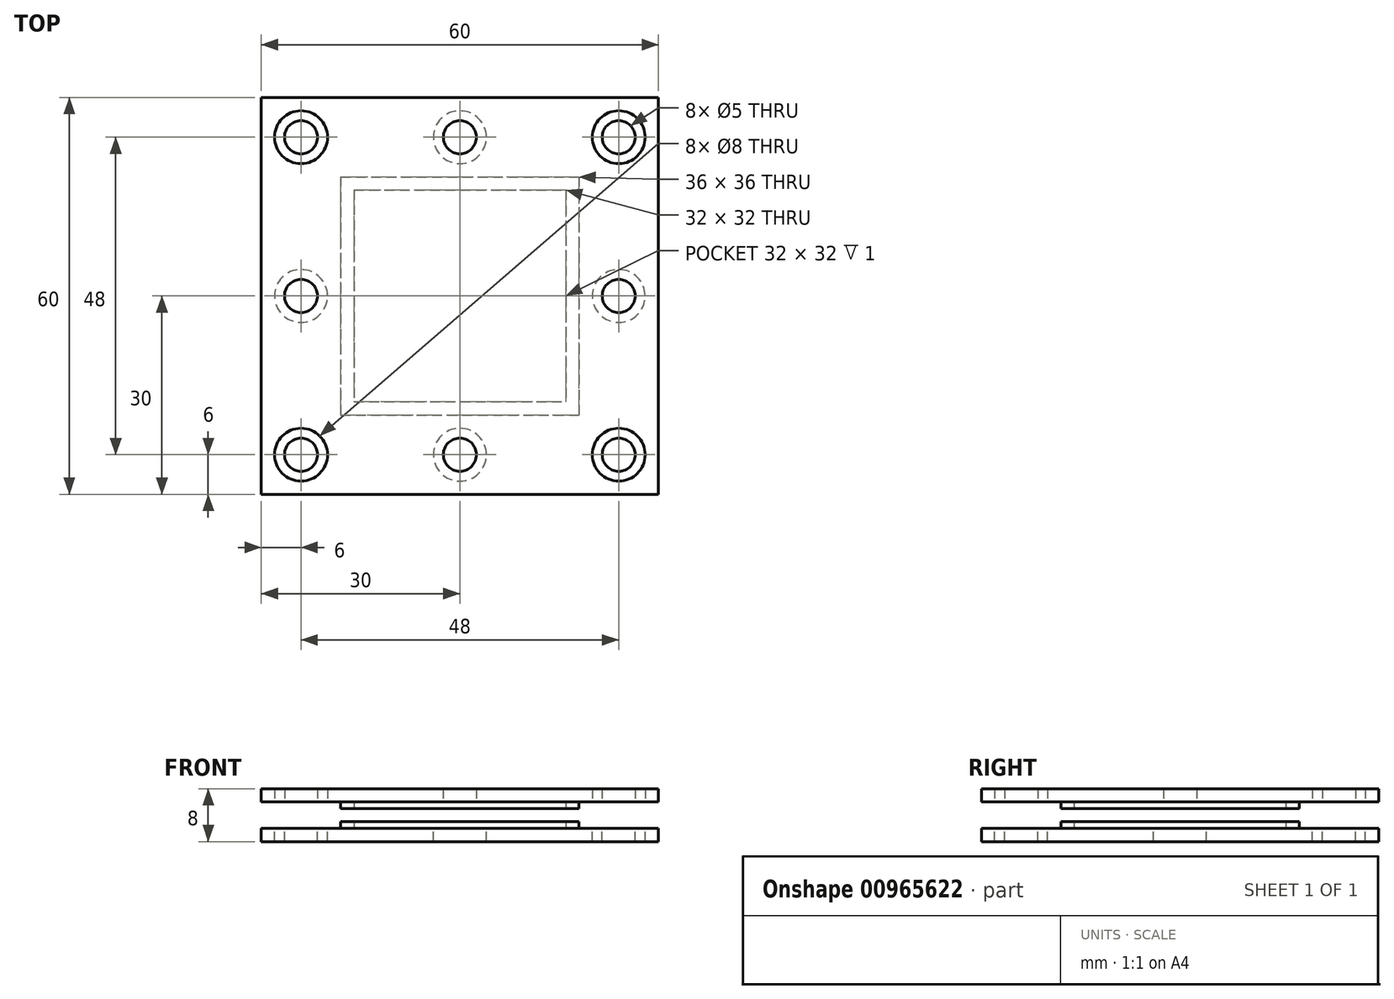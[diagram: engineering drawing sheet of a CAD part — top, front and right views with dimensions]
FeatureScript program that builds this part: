
annotation { "Feature Type Name" : "Feature", "Feature Type Description" : "" }
export const myFeature = defineFeature(function(context is Context, id is Id, definition is map)
    precondition{}
    {
        {
            var Q0;
            Q0=qCreatedBy(makeId("Top.planeOp"),FACE);
            var sketch = newSketch(context, id + "F0", { "sketchPlane" : qUnion([Q0])});
            skLineSegment(sketch, "E0.bottom", {"start": v(-16, 16) * mm, "end": v(16, 16) * mm});
            skLineSegment(sketch, "E0.top", {"start": v(-16, -16) * mm, "end": v(16, -16) * mm});
            skLineSegment(sketch, "E0.left", {"start": v(-16, 16) * mm, "end": v(-16, -16) * mm});
            skLineSegment(sketch, "E0.right", {"start": v(16, 16) * mm, "end": v(16, -16) * mm});
            skPoint(sketch, "E0.middle", {"position": v(0, 0) * mm});
            skLineSegment(sketch, "E1.bottom", {"start": v(-18, 18) * mm, "end": v(18, 18) * mm});
            skLineSegment(sketch, "E1.top", {"start": v(-18, -18) * mm, "end": v(18, -18) * mm});
            skLineSegment(sketch, "E1.left", {"start": v(-18, 18) * mm, "end": v(-18, -18) * mm});
            skLineSegment(sketch, "E1.right", {"start": v(18, 18) * mm, "end": v(18, -18) * mm});
            skLineSegment(sketch, "E2.bottom", {"start": v(-30, 30) * mm, "end": v(30, 30) * mm});
            skLineSegment(sketch, "E2.top", {"start": v(-30, -30) * mm, "end": v(30, -30) * mm});
            skLineSegment(sketch, "E2.left", {"start": v(-30, 30) * mm, "end": v(-30, -30) * mm});
            skLineSegment(sketch, "E2.right", {"start": v(30, 30) * mm, "end": v(30, -30) * mm});
            skCircle(sketch, "E3", {"center": v(-24, 24) * mm, "radius": 2.5 * mm});
            skCircle(sketch, "E4", {"center": v(24, 24) * mm, "radius": 2.5 * mm});
            skCircle(sketch, "E5", {"center": v(24, -24) * mm, "radius": 2.5 * mm});
            skCircle(sketch, "E6", {"center": v(-24, -24) * mm, "radius": 2.5 * mm});
            skCircle(sketch, "E7", {"center": v(24, 0) * mm, "radius": 2.5 * mm});
            skCircle(sketch, "E8", {"center": v(0, 24) * mm, "radius": 2.5 * mm});
            skCircle(sketch, "E9", {"center": v(-24, 0) * mm, "radius": 2.5 * mm});
            skCircle(sketch, "E10", {"center": v(0, -24) * mm, "radius": 2.5 * mm});
            skCircle(sketch, "E11", {"center": v(-24, 24) * mm, "radius": 4 * mm});
            skCircle(sketch, "E12", {"center": v(-24, 0) * mm, "radius": 4 * mm});
            skCircle(sketch, "E13", {"center": v(-24, -24) * mm, "radius": 4 * mm});
            skCircle(sketch, "E14", {"center": v(0, -24) * mm, "radius": 4 * mm});
            skCircle(sketch, "E15", {"center": v(24, -24) * mm, "radius": 4 * mm});
            skCircle(sketch, "E16", {"center": v(24, 0) * mm, "radius": 4 * mm});
            skCircle(sketch, "E17", {"center": v(24, 24) * mm, "radius": 4 * mm});
            skCircle(sketch, "E18", {"center": v(0, 24) * mm, "radius": 4 * mm});
            skSolve(sketch);
        }
        {
            var Q0;
            Q0=makeQuery(id+"F0.imprint","IMPRINT",FACE,{"disambiguationData":[TD([[makeQuery(id+"F0.imprint","IMPRINT",EDGE,{"derivedFrom":sQuery(id+"F0.wireOp",EDGE,"E1.bottom")}),1.0]])]});
            var Q1;
            Q1=makeQuery(id+"F0.imprint","IMPRINT",FACE,{"disambiguationData":[TD([[makeQuery(id+"F0.imprint","IMPRINT",EDGE,{"derivedFrom":sQuery(id+"F0.wireOp",EDGE,"E0.bottom")}),1.0]])]});
            var Q2;
            Q2=makeQuery(id+"F0.imprint","IMPRINT",FACE,{"disambiguationData":[TD([[makeQuery(id+"F0.imprint","IMPRINT",EDGE,{"derivedFrom":sQuery(id+"F0.wireOp",EDGE,"E0.bottom")}),-1.0]])]});
            var Q3;
            Q3=makeQuery(id+"F0.imprint","IMPRINT",FACE,{"disambiguationData":[TD([[makeQuery(id+"F0.imprint","IMPRINT",EDGE,{"derivedFrom":sQuery(id+"F0.wireOp",EDGE,"E3")}),-1.0]])]});
            var Q4;
            Q4=makeQuery(id+"F0.imprint","IMPRINT",FACE,{"disambiguationData":[TD([[makeQuery(id+"F0.imprint","IMPRINT",EDGE,{"derivedFrom":sQuery(id+"F0.wireOp",EDGE,"E4")}),-1.0]])]});
            var Q5;
            Q5=makeQuery(id+"F0.imprint","IMPRINT",FACE,{"disambiguationData":[TD([[makeQuery(id+"F0.imprint","IMPRINT",EDGE,{"derivedFrom":sQuery(id+"F0.wireOp",EDGE,"E5")}),-1.0]])]});
            var Q6;
            Q6=makeQuery(id+"F0.imprint","IMPRINT",FACE,{"disambiguationData":[TD([[makeQuery(id+"F0.imprint","IMPRINT",EDGE,{"derivedFrom":sQuery(id+"F0.wireOp",EDGE,"E6")}),-1.0]])]});
            extrude(context, id + "F1", {"entities" : qUnion([Q0, Q1, Q2, Q3, Q4, Q5, Q6]), "oppositeDirection" : true, "depth" : 2 * mm, "offsetDistance" : 25 * mm});
        }
        {
            var Q0;
            Q0=makeQuery(id+"F0.imprint","IMPRINT",FACE,{"disambiguationData":[TD([[makeQuery(id+"F0.imprint","IMPRINT",EDGE,{"derivedFrom":sQuery(id+"F0.wireOp",EDGE,"E0.bottom")}),1.0]])]});
            extrude(context, id + "F2", {"entities" : qUnion([Q0]), "operationType" : NewBodyOperationType.ADD, "depth" : 1 * mm, "offsetDistance" : 25 * mm});
        }
        {
            var Q0;
            Q0=makeQuery(id+"F0.imprint","IMPRINT",FACE,{"disambiguationData":[TD([[makeQuery(id+"F0.imprint","IMPRINT",EDGE,{"derivedFrom":sQuery(id+"F0.wireOp",EDGE,"E1.bottom")}),1.0]])]});
            var Q1;
            Q1=makeQuery(id+"F0.imprint","IMPRINT",FACE,{"disambiguationData":[TD([[makeQuery(id+"F0.imprint","IMPRINT",EDGE,{"derivedFrom":sQuery(id+"F0.wireOp",EDGE,"E9")}),-1.0]])]});
            var Q2;
            Q2=makeQuery(id+"F0.imprint","IMPRINT",FACE,{"disambiguationData":[TD([[makeQuery(id+"F0.imprint","IMPRINT",EDGE,{"derivedFrom":sQuery(id+"F0.wireOp",EDGE,"E8")}),-1.0]])]});
            var Q3;
            Q3=makeQuery(id+"F0.imprint","IMPRINT",FACE,{"disambiguationData":[TD([[makeQuery(id+"F0.imprint","IMPRINT",EDGE,{"derivedFrom":sQuery(id+"F0.wireOp",EDGE,"E7")}),-1.0]])]});
            var Q4;
            Q4=makeQuery(id+"F0.imprint","IMPRINT",FACE,{"disambiguationData":[TD([[makeQuery(id+"F0.imprint","IMPRINT",EDGE,{"derivedFrom":sQuery(id+"F0.wireOp",EDGE,"E10")}),-1.0]])]});
            var Q5;
            Q5=makeQuery(id+"F0.imprint","IMPRINT",FACE,{"disambiguationData":[TD([[makeQuery(id+"F0.imprint","IMPRINT",EDGE,{"derivedFrom":sQuery(id+"F0.wireOp",EDGE,"E0.bottom")}),-1.0]])]});
            var Q6;
            Q6=makeQuery(id+"F0.imprint","IMPRINT",FACE,{"disambiguationData":[TD([[makeQuery(id+"F0.imprint","IMPRINT",EDGE,{"derivedFrom":sQuery(id+"F0.wireOp",EDGE,"E0.bottom")}),1.0]])]});
            extrude(context, id + "F3", {"entities" : qUnion([Q0, Q1, Q2, Q3, Q4, Q5, Q6]), "depth" : 6 * mm, "offsetDistance" : 25 * mm, "hasSecondDirection" : true, "secondDirectionOppositeDirection" : false, "secondDirectionDepth" : 4 * mm});
        }
        {
            var Q0;
            Q0=makeQuery(id+"F0.imprint","IMPRINT",FACE,{"disambiguationData":[TD([[makeQuery(id+"F0.imprint","IMPRINT",EDGE,{"derivedFrom":sQuery(id+"F0.wireOp",EDGE,"E0.bottom")}),1.0]])]});
            extrude(context, id + "F4", {"entities" : qUnion([Q0]), "operationType" : NewBodyOperationType.ADD, "depth" : 4 * mm, "offsetDistance" : 25 * mm, "hasSecondDirection" : true, "secondDirectionOppositeDirection" : false, "secondDirectionDepth" : 3 * mm});
        }
    });
